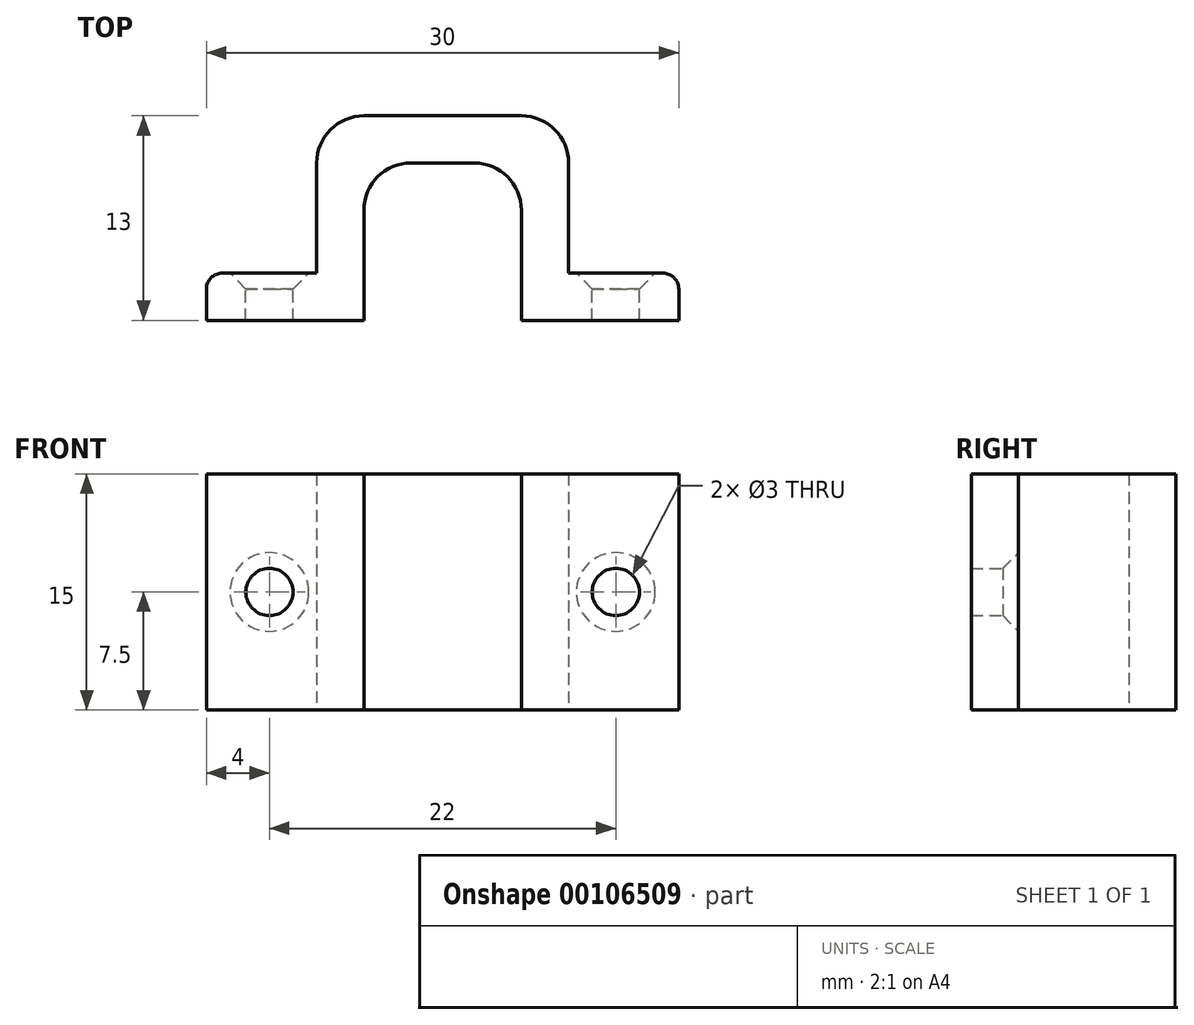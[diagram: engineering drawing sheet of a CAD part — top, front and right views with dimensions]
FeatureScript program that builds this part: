
annotation { "Feature Type Name" : "Feature", "Feature Type Description" : "" }
export const myFeature = defineFeature(function(context is Context, id is Id, definition is map)
    precondition{}
    {
        {
            var Q0;
            Q0=qCreatedBy(makeId("Top.planeOp"),FACE);
            var sketch = newSketch(context, id + "F0", { "sketchPlane" : qUnion([Q0])});
            skLineSegment(sketch, "E0", {"start": v(5, 0) * mm, "end": v(5, 7) * mm});
            skLineSegment(sketch, "E1", {"start": v(8, 3) * mm, "end": v(14, 3) * mm});
            skLineSegment(sketch, "E2", {"start": v(15, 2) * mm, "end": v(15, 0) * mm});
            skLineSegment(sketch, "E3", {"start": v(15, 0) * mm, "end": v(5, 0) * mm});
            skLineSegment(sketch, "E4", {"start": v(2, 10) * mm, "end": v(0, 10) * mm});
            skLineSegment(sketch, "E5", {"start": v(0, 10) * mm, "end": v(0, 13) * mm});
            skLineSegment(sketch, "E6", {"start": v(0, 13) * mm, "end": v(5, 13) * mm});
            skLineSegment(sketch, "E7", {"start": v(8, 3) * mm, "end": v(8, 10) * mm});
            skPoint(sketch, "E8.visualSharp", {"position": v(8, 13) * mm});
            skArc(sketch, "E8.filletArc", {"start": v(8, 10) * mm, "mid": v(7.12, 12.12) * mm, "end": v(5, 13) * mm});
            skArc(sketch, "E9.filletArc", {"start": v(5, 7) * mm, "mid": v(4.12, 9.12) * mm, "end": v(2, 10) * mm});
            skPoint(sketch, "E10.visualSharp", {"position": v(15, 3) * mm});
            skArc(sketch, "E10.filletArc", {"start": v(15, 2) * mm, "mid": v(14.7, 2.7) * mm, "end": v(14, 3) * mm});
            skArc(sketch, "E11.MirrorCS", {"start": v(-15, 2) * mm, "mid": v(-14.7, 2.7) * mm, "end": v(-14, 3) * mm});
            skLineSegment(sketch, "E12.MirrorCS", {"start": v(-15, 2) * mm, "end": v(-15, 0) * mm});
            skPoint(sketch, "E13.MirrorP", {"position": v(-15, 3) * mm});
            skLineSegment(sketch, "E14.MirrorCS", {"start": v(-8, 3) * mm, "end": v(-14, 3) * mm});
            skPoint(sketch, "E15.MirrorP", {"position": v(-5, 10) * mm});
            skLineSegment(sketch, "E16.MirrorCS", {"start": v(-15, 0) * mm, "end": v(-5, 0) * mm});
            skArc(sketch, "E17.MirrorCS", {"start": v(-5, 7) * mm, "mid": v(-4.12, 9.12) * mm, "end": v(-2, 10) * mm});
            skArc(sketch, "E18.MirrorCS", {"start": v(-8, 10) * mm, "mid": v(-7.12, 12.12) * mm, "end": v(-5, 13) * mm});
            skLineSegment(sketch, "E19.MirrorCS", {"start": v(-8, 3) * mm, "end": v(-8, 10) * mm});
            skLineSegment(sketch, "E20.MirrorCS", {"start": v(0, 13) * mm, "end": v(-5, 13) * mm});
            skLineSegment(sketch, "E21.MirrorCS", {"start": v(-2, 10) * mm, "end": v(0, 10) * mm});
            skLineSegment(sketch, "E22.MirrorCS", {"start": v(-5, 0) * mm, "end": v(-5, 7) * mm});
            skPoint(sketch, "E23.MirrorP", {"position": v(-8, 13) * mm});
            skSolve(sketch);
        }
        {
            var Q0;
            Q0 = qSketchRegion(id + "F0", true);
            extrude(context, id + "F1", {"entities" : qUnion([Q0]), "depth" : 15 * mm});
        }
        {
            var Q0;
            Q0=qCreatedBy(makeId("Front.planeOp"),FACE);
            cPlane(context, id + "F2", {"entities" : qUnion([Q0]), "cplaneType" : CPlaneType.OFFSET, "offset" : 3 * mm, "oppositeDirection" : true, "width" : 150 * mm, "height" : 150 * mm});
        }
        {
            var Q0;
            Q0=qCreatedBy(id+"F2.planeOp",FACE);
            var sketch = newSketch(context, id + "F3", { "sketchPlane" : qUnion([Q0])});
            skPoint(sketch, "E24", {"position": v(-11, 7.5) * mm});
            skPoint(sketch, "E25.MirrorP", {"position": v(11, 7.5) * mm});
            skSolve(sketch);
        }
        {
            var Q0;
            Q0=sQuery(id+"F3.wireOp",VERTEX,"E25.MirrorP");
            var Q1;
            Q1=sQuery(id+"F3.wireOp",VERTEX,"E24");
            var Q2;
            Q2=makeQuery(id+"F1.opExtrude","SWEPT_BODY",BODY,{"disambiguationData":[OSD([sQuery(id+"F0.wireOp",EDGE,"E0"),sQuery(id+"F0.wireOp",EDGE,"E1"),sQuery(id+"F0.wireOp",EDGE,"E2"),sQuery(id+"F0.wireOp",EDGE,"E3"),sQuery(id+"F0.wireOp",EDGE,"E4"),sQuery(id+"F0.wireOp",EDGE,"E6"),sQuery(id+"F0.wireOp",EDGE,"E7"),sQuery(id+"F0.wireOp",EDGE,"E8.filletArc"),sQuery(id+"F0.wireOp",EDGE,"E9.filletArc"),sQuery(id+"F0.wireOp",EDGE,"E10.filletArc"),sQuery(id+"F0.wireOp",EDGE,"E11.MirrorCS"),sQuery(id+"F0.wireOp",EDGE,"E12.MirrorCS"),sQuery(id+"F0.wireOp",EDGE,"E14.MirrorCS"),sQuery(id+"F0.wireOp",EDGE,"E16.MirrorCS"),sQuery(id+"F0.wireOp",EDGE,"E17.MirrorCS"),sQuery(id+"F0.wireOp",EDGE,"E18.MirrorCS"),sQuery(id+"F0.wireOp",EDGE,"E19.MirrorCS"),sQuery(id+"F0.wireOp",EDGE,"E20.MirrorCS"),sQuery(id+"F0.wireOp",EDGE,"E21.MirrorCS"),sQuery(id+"F0.wireOp",EDGE,"E22.MirrorCS")])]});
            hole(context, id + "F4", {"style" : HoleStyle.C_SINK, "endStyle" : HoleEndStyle.BLIND, "oppositeDirection" : true, "holeDiameter" : 3 * mm, "cSinkDiameter" : 5 * mm, "cSinkAngle" : 90 * degree, "holeDepth" : 3 * mm, "locations" : qUnion([Q0, Q1]), "scope" : qUnion([Q2])});
        }
    });
